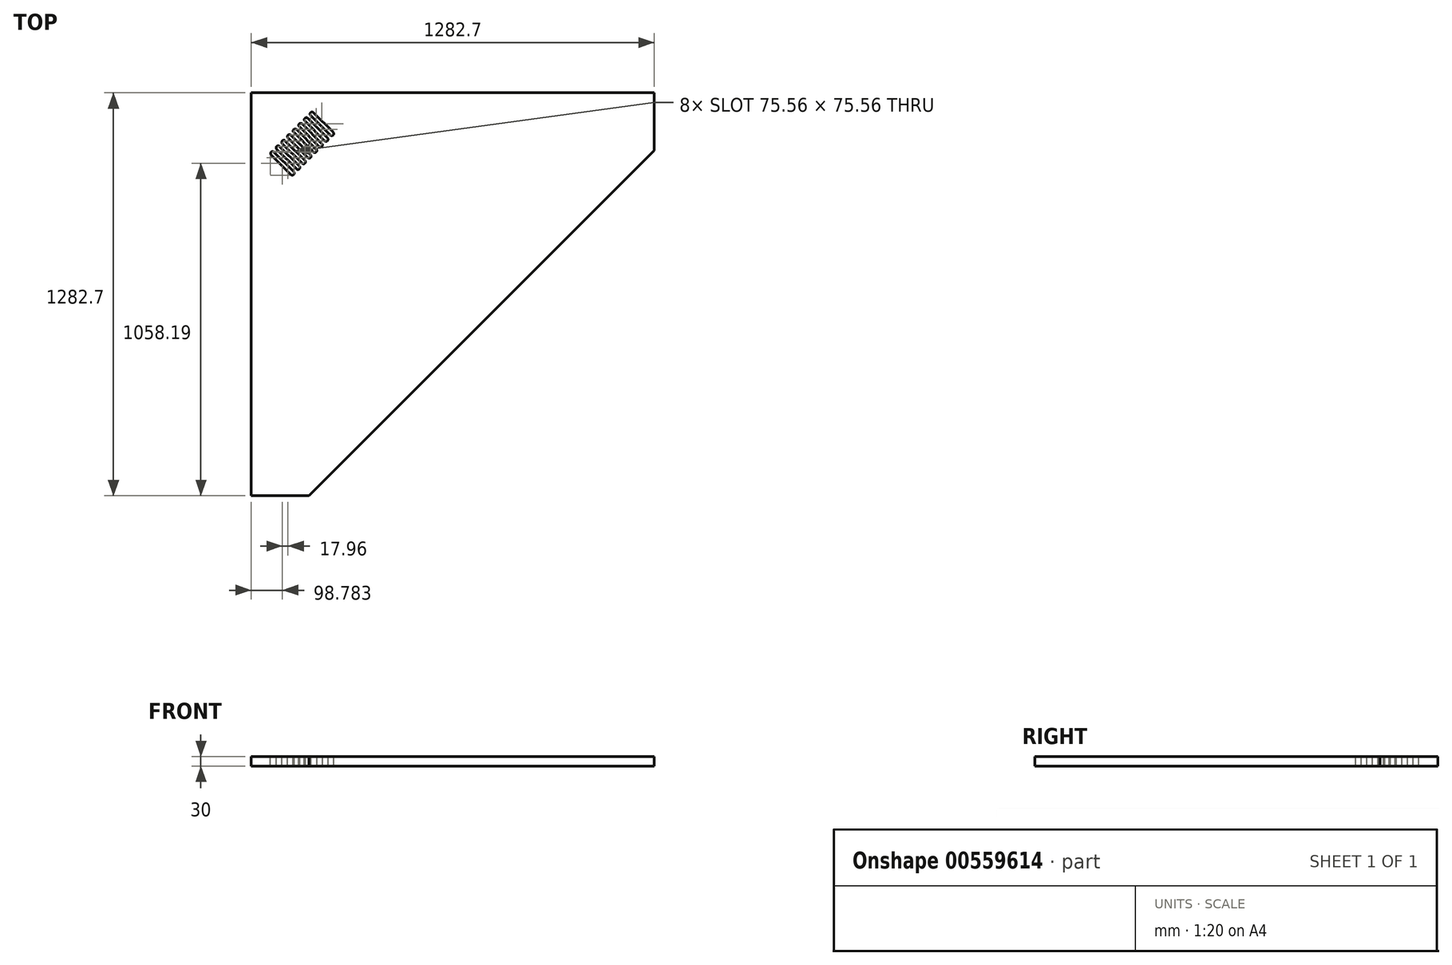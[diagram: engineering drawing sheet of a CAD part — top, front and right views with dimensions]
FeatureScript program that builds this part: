
annotation { "Feature Type Name" : "Feature", "Feature Type Description" : "" }
export const myFeature = defineFeature(function(context is Context, id is Id, definition is map)
    precondition{}
    {
        {
            var Q0;
            Q0=qCreatedBy(makeId("Top.planeOp"),FACE);
            var sketch = newSketch(context, id + "F0", { "sketchPlane" : qUnion([Q0])});
            skLineSegment(sketch, "E0.bottom", {"start": v(-641.35, 641.35) * mm, "end": v(641.35, 641.35) * mm});
            skLineSegment(sketch, "E0.top", {"start": v(-641.35, -641.35) * mm, "end": v(641.35, -641.35) * mm, "construction": true});
            skLineSegment(sketch, "E0.left", {"start": v(-641.35, 641.35) * mm, "end": v(-641.35, -641.35) * mm});
            skLineSegment(sketch, "E0.right", {"start": v(641.35, 641.35) * mm, "end": v(641.35, -641.35) * mm, "construction": true});
            skPoint(sketch, "E0.middle", {"position": v(0, 0) * mm});
            skLineSegment(sketch, "E1", {"start": v(641.35, 641.35) * mm, "end": v(641.35, 457.2) * mm});
            skLineSegment(sketch, "E2", {"start": v(641.35, 457.2) * mm, "end": v(-457.2, -641.35) * mm});
            skLineSegment(sketch, "E3", {"start": v(-457.2, -641.35) * mm, "end": v(-641.35, -641.35) * mm});
            skSolve(sketch);
        }
        {
            var Q0;
            Q0 = qSketchRegion(id + "F0", true);
            extrude(context, id + "F1", {"entities" : qUnion([Q0]), "depth" : 30 * mm, "offsetDistance" : 25.4 * mm});
        }
        {
            var Q0;
            Q0=makeQuery(id+"F1.opExtrude","CAP_FACE",FACE,{"disambiguationData":[OSD([sQuery(id+"F0.wireOp",EDGE,"E0.bottom"),sQuery(id+"F0.wireOp",EDGE,"E0.left"),sQuery(id+"F0.wireOp",EDGE,"E1"),sQuery(id+"F0.wireOp",EDGE,"E2"),sQuery(id+"F0.wireOp",EDGE,"E3")])],"isStart":false});
            var sketch = newSketch(context, id + "F2", { "sketchPlane" : qUnion([Q0])});
            skLineSegment(sketch, "E4", {"start": v(-448.27, 582.98) * mm, "end": v(-582.98, 448.27) * mm, "construction": true});
            skLineSegment(sketch, "E5", {"start": v(-582.98, 448.27) * mm, "end": v(-511.14, 376.43) * mm, "construction": true});
            skLineSegment(sketch, "E6", {"start": v(-511.14, 376.43) * mm, "end": v(-376.43, 511.14) * mm, "construction": true});
            skLineSegment(sketch, "E7", {"start": v(-376.43, 511.14) * mm, "end": v(-448.27, 582.98) * mm, "construction": true});
            skArc(sketch, "E8", {"start": v(-569.5, 452.76) * mm, "mid": v(-578.49, 452.76) * mm, "end": v(-578.49, 443.78) * mm});
            skArc(sketch, "E9", {"start": v(-515.63, 380.92) * mm, "mid": v(-506.65, 380.92) * mm, "end": v(-506.65, 389.9) * mm});
            skLineSegment(sketch, "E10", {"start": v(-578.49, 443.78) * mm, "end": v(-515.63, 380.92) * mm});
            skLineSegment(sketch, "E11", {"start": v(-506.65, 389.9) * mm, "end": v(-569.5, 452.76) * mm});
            skArc(sketch, "E12", {"start": v(-551.55, 470.73) * mm, "mid": v(-560.53, 470.73) * mm, "end": v(-560.53, 461.74) * mm});
            skArc(sketch, "E13", {"start": v(-497.67, 398.88) * mm, "mid": v(-488.69, 398.88) * mm, "end": v(-488.69, 407.86) * mm});
            skArc(sketch, "E14", {"start": v(-479.7, 416.84) * mm, "mid": v(-470.73, 416.84) * mm, "end": v(-470.73, 425.82) * mm});
            skArc(sketch, "E15", {"start": v(-533.59, 488.69) * mm, "mid": v(-542.57, 488.69) * mm, "end": v(-542.57, 479.7) * mm});
            skArc(sketch, "E16", {"start": v(-515.63, 506.65) * mm, "mid": v(-524.6, 506.65) * mm, "end": v(-524.6, 497.67) * mm});
            skArc(sketch, "E17", {"start": v(-461.74, 434.8) * mm, "mid": v(-452.76, 434.8) * mm, "end": v(-452.76, 443.78) * mm});
            skArc(sketch, "E18", {"start": v(-443.78, 452.76) * mm, "mid": v(-434.8, 452.76) * mm, "end": v(-434.8, 461.74) * mm});
            skArc(sketch, "E19", {"start": v(-497.67, 524.6) * mm, "mid": v(-506.65, 524.6) * mm, "end": v(-506.65, 515.63) * mm});
            skArc(sketch, "E20", {"start": v(-425.82, 470.73) * mm, "mid": v(-416.84, 470.73) * mm, "end": v(-416.84, 479.7) * mm});
            skArc(sketch, "E21", {"start": v(-479.7, 542.57) * mm, "mid": v(-488.69, 542.57) * mm, "end": v(-488.69, 533.59) * mm});
            skArc(sketch, "E22", {"start": v(-407.86, 488.69) * mm, "mid": v(-398.88, 488.69) * mm, "end": v(-398.88, 497.67) * mm});
            skArc(sketch, "E23", {"start": v(-461.74, 560.53) * mm, "mid": v(-470.73, 560.53) * mm, "end": v(-470.73, 551.55) * mm});
            skArc(sketch, "E24", {"start": v(-443.78, 578.49) * mm, "mid": v(-452.76, 578.49) * mm, "end": v(-452.76, 569.5) * mm});
            skArc(sketch, "E25", {"start": v(-389.9, 506.65) * mm, "mid": v(-380.92, 506.65) * mm, "end": v(-380.92, 515.63) * mm});
            skLineSegment(sketch, "E26", {"start": v(-542.57, 479.7) * mm, "end": v(-479.7, 416.84) * mm});
            skLineSegment(sketch, "E27", {"start": v(-470.73, 425.82) * mm, "end": v(-533.59, 488.69) * mm});
            skLineSegment(sketch, "E28", {"start": v(-524.6, 497.67) * mm, "end": v(-461.74, 434.8) * mm});
            skLineSegment(sketch, "E29", {"start": v(-452.76, 443.78) * mm, "end": v(-515.63, 506.65) * mm});
            skLineSegment(sketch, "E30", {"start": v(-506.65, 515.63) * mm, "end": v(-443.78, 452.76) * mm});
            skLineSegment(sketch, "E31", {"start": v(-434.8, 461.74) * mm, "end": v(-497.67, 524.6) * mm});
            skLineSegment(sketch, "E32", {"start": v(-488.69, 533.59) * mm, "end": v(-425.82, 470.73) * mm});
            skLineSegment(sketch, "E33", {"start": v(-416.84, 479.7) * mm, "end": v(-479.7, 542.57) * mm});
            skLineSegment(sketch, "E34", {"start": v(-398.88, 497.67) * mm, "end": v(-461.74, 560.53) * mm});
            skLineSegment(sketch, "E35", {"start": v(-380.92, 515.63) * mm, "end": v(-443.78, 578.49) * mm});
            skLineSegment(sketch, "E36", {"start": v(-470.73, 551.55) * mm, "end": v(-407.86, 488.69) * mm});
            skLineSegment(sketch, "E37", {"start": v(-389.9, 506.65) * mm, "end": v(-452.76, 569.5) * mm});
            skLineSegment(sketch, "E38", {"start": v(-560.53, 461.74) * mm, "end": v(-497.67, 398.88) * mm});
            skLineSegment(sketch, "E39", {"start": v(-551.55, 470.73) * mm, "end": v(-488.69, 407.86) * mm});
            skSolve(sketch);
        }
        {
            var Q0;
            Q0 = qSketchRegion(id + "F2", true);
            extrude(context, id + "F3", {"entities" : qUnion([Q0]), "operationType" : NewBodyOperationType.REMOVE, "endBound" : BoundingType.UP_TO_NEXT, "oppositeDirection" : true, "depth" : 25.4 * mm, "offsetDistance" : 25.4 * mm});
        }
    });
